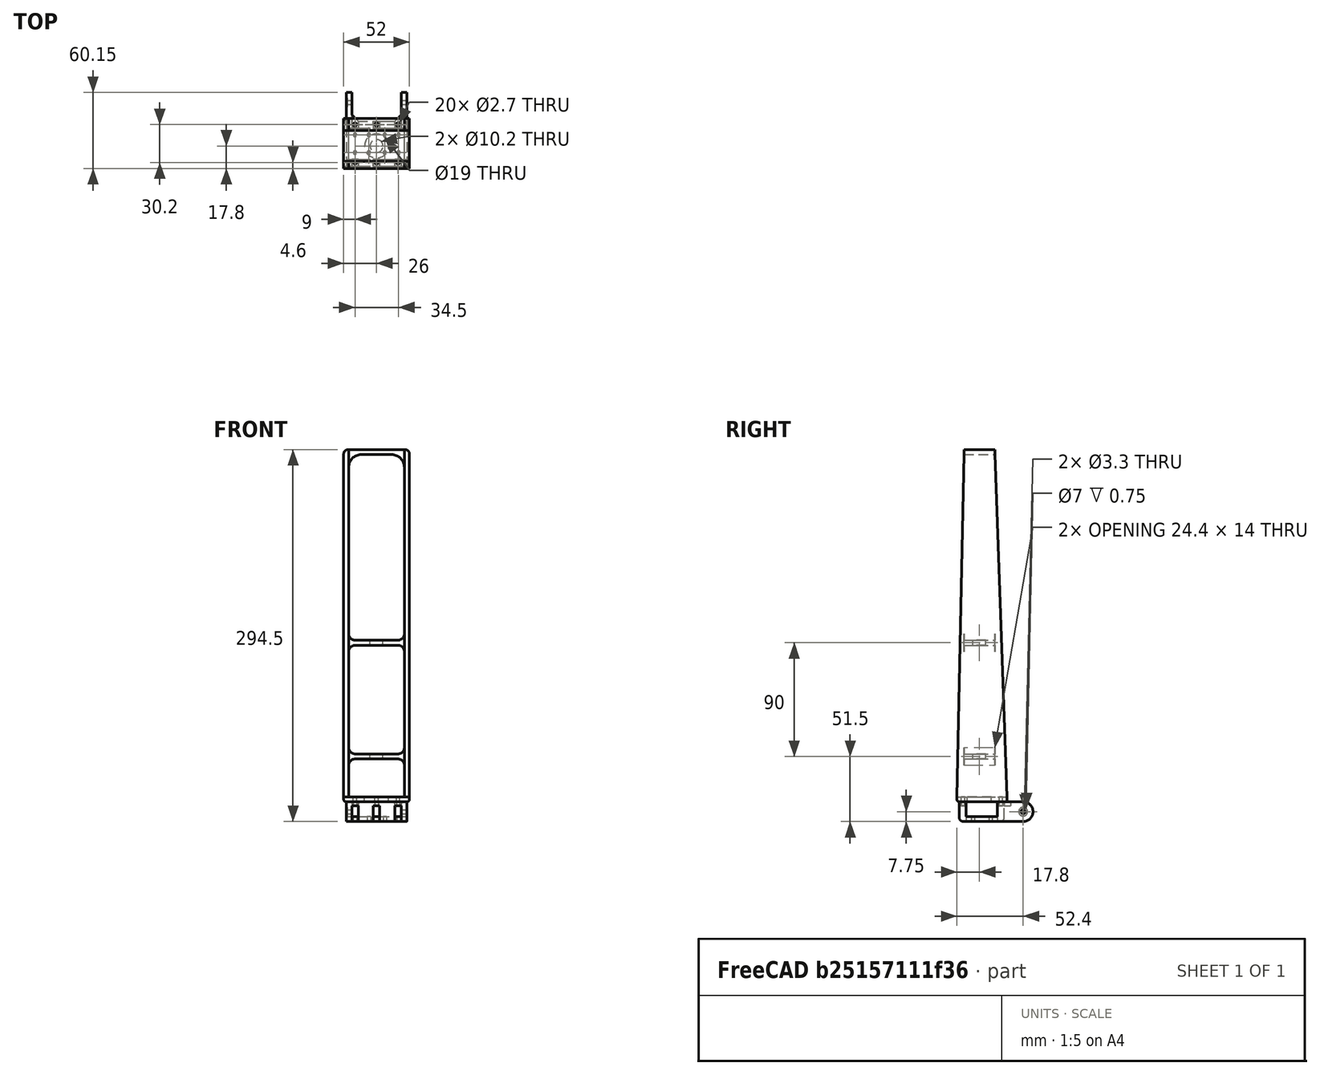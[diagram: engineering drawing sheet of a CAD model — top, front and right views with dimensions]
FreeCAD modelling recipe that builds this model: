
FCSTD DOCUMENT  (FreeCAD 0.16R6705 (Git))
Label: upper_arm_dummy
License: All rights reserved
LicenseURL: http://en.wikipedia.org/wiki/All_rights_reserved
objects: Part::Box×10, Part::MultiFuse×9, Part::Cylinder×8, Part::Fillet×6, Part::Cut×3, Part::Wedge×1, Part::Mirroring×1, Part::Feature×1
note: 39 computed .brp shape members not serialized (recipe doc carries the construction recipe); baked Part::Feature solids carry a one-line shape summary decoded from their .brp

FEATURE [Part::Box] Box  label="Cube"
  Height = 4
  Length = 52
  Placement = pos=(-2,-2,0) rot=(0,0,1;0rad)
  Width = 39.6
FEATURE [Part::Cylinder] Cylinder
  Angle = 360
  Height = 20
  Placement = pos=(6,2.8,-2) rot=(0,0,1;0rad)
  Radius = 1.35
FEATURE [Part::Cylinder] Cylinder001
  Angle = 360
  Height = 20
  Placement = pos=(6,2.8,-2) rot=(0,0,1;0rad)
  Radius = 1.35
FEATURE [Part::Cylinder] Cylinder002
  Angle = 360
  Height = 20
  Placement = pos=(6,2.8,-2) rot=(0,0,1;0rad)
  Radius = 1.35
FEATURE [Part::Cylinder] Cylinder003
  Angle = 360
  Height = 20
  Placement = pos=(6,32.8,-2) rot=(0,0,1;0rad)
  Radius = 1.35
FEATURE [Part::Cylinder] Cylinder004
  Angle = 360
  Height = 20
  Placement = pos=(6,32.8,-2) rot=(0,0,1;0rad)
  Radius = 1.35
FEATURE [Part::Cylinder] Cylinder005
  Angle = 360
  Height = 20
  Placement = pos=(6,32.8,-2) rot=(0,0,1;0rad)
  Radius = 1.35
FEATURE [Part::Box] Box005
  Height = 20
  Length = 5
  Placement = pos=(3.5,30.2,3) rot=(0,0,1;0rad)
  Width = 8
FEATURE [Part::Box] Box006
  Height = 20
  Length = 5
  Placement = pos=(3.5,30.2,3) rot=(0,0,1;0rad)
  Width = 8
FEATURE [Part::Box] Box007
  Height = 20
  Length = 5
  Placement = pos=(3.5,30.2,3) rot=(0,0,1;0rad)
  Width = 8
FEATURE [Part::Box] Box002
  Height = 20
  Length = 5
  Placement = pos=(3.5,-2.6,3) rot=(0,0,1;0rad)
  Width = 8
FEATURE [Part::Box] Box004
  Height = 20
  Length = 5
  Placement = pos=(3.5,-2.6,3) rot=(0,0,1;0rad)
  Width = 8
FEATURE [Part::Box] Box003
  Height = 20
  Length = 5
  Placement = pos=(3.5,-2.6,3) rot=(0,0,1;0rad)
  Width = 8
FEATURE [Part::MultiFuse] Fusion002
  Placement = pos=(34,0,0) rot=(0,0,1;0rad)
  Shapes = -> [Box004,Cylinder002]
FEATURE [Part::MultiFuse] Fusion003
  Shapes = -> [Cylinder003,Box005]
FEATURE [Part::MultiFuse] Fusion004
  Placement = pos=(17,0,0) rot=(0,0,1;0rad)
  Shapes = -> [Cylinder004,Box006]
FEATURE [Part::MultiFuse] Fusion005
  Placement = pos=(34,0,0) rot=(0,0,1;0rad)
  Shapes = -> [Cylinder005,Box007]
FEATURE [Part::MultiFuse] Fusion
  Shapes = -> [Box002,Cylinder]
FEATURE [Part::MultiFuse] Fusion001
  Placement = pos=(17,0,0) rot=(0,0,1;0rad)
  Shapes = -> [Box003,Cylinder001]
FEATURE [Part::MultiFuse] Fusion006
  Placement = pos=(1,0,1) rot=(0,0,1;0rad)
  Shapes = -> [Fusion002,Fusion003,Fusion004,Fusion005,Fusion,Fusion001]
FEATURE [Part::Cut] Cut
  Base = -> Box
  Placement = pos=(0,0,-4) rot=(0,0,1;0rad)
  Tool = -> Fusion006
FEATURE [Part::Wedge] Wedge
  Placement = pos=(-2,-2,275) rot=(-1,0,0;1.5708rad)
  X2max = 4
  X2min = 0
  Xmax = 4
  Xmin = 0
  Ymax = 275
  Ymin = 0
  Z2max = 39.6
  Z2min = 0
  Zmax = 30
  Zmin = 5.6
FEATURE [Part::Mirroring] Part__Mirroring  label="Wedge (Mirror #1)"
  Base = (24,0,0)
  Normal = (1,0,0)
  Source = -> Wedge
FEATURE [Part::Box] Box008  label="Cube001"
  Height = 4
  Length = 44
  Placement = pos=(2,3.6,30) rot=(0,0,1;0rad)
  Width = 24.4
FEATURE [Part::Box] Box009  label="Cube002"
  Height = 4
  Length = 44
  Placement = pos=(2,3.6,120) rot=(0,0,1;0rad)
  Width = 24.4
FEATURE [Part::Box] Box010  label="Cube003"
  Height = 4
  Length = 44
  Placement = pos=(2,3.6,271) rot=(0,0,1;0rad)
  Width = 24.4
FEATURE [Part::MultiFuse] Fusion007
  Shapes = -> [Cut,Part__Mirroring,Box008,Box009,Box010,Wedge]
FEATURE [Part::Fillet] Fillet
  Base = -> Fusion007
  Edges = 4 edges r=2: [Edge15,Edge38,Edge47,Edge57]
FEATURE [Part::Fillet] Fillet001
  Base = -> Fillet
  Edges = 1 edges r=10: [Edge94]
FEATURE [Part::Fillet] Fillet002
  Base = -> Fillet001
  Edges = 1 edges r=10: [Edge75]
FEATURE [Part::Fillet] Fillet003
  Base = -> Fillet002
  Edges = 2 edges r=3.5: [Edge91,Edge92]
FEATURE [Part::Fillet] Fillet004
  Base = -> Fillet003
  Edges = 4 edges r=5: [Edge36,Edge37,Edge103,Edge105]
FEATURE [Part::Fillet] Fillet005
  Base = -> Fillet003
  Edges = 4 edges r=5: [Edge31,Edge34,Edge92,Edge99]
FEATURE [Part::Cylinder] Cylinder006
  Angle = 360
  Height = 150
  Placement = pos=(24,15.8,15) rot=(0,0,1;0rad)
  Radius = 5.1
FEATURE [Part::MultiFuse] Fusion008
  Shapes = -> [Fillet004,Fillet005]
FEATURE [Part::Cut] Cut001
  Base = -> Fusion008
  Tool = -> Cylinder006
FEATURE [Part::Cylinder] Cylinder007
  Angle = 360
  Height = 30
  Placement = pos=(24,15.8,-20) rot=(0,0,1;0rad)
  Radius = 9.5
FEATURE [Part::Cut] Cut002
  Base = -> Cut001
  Tool = -> Cylinder007
FEATURE [Part::Feature] Part__Feature  label="Chamfer"
  Placement = pos=(1,35.4,-4) rot=(1,0,0;3.14159rad)
  shape: bbox 48 x 58.35 x 15.5 mm, 85 faces (baked)
